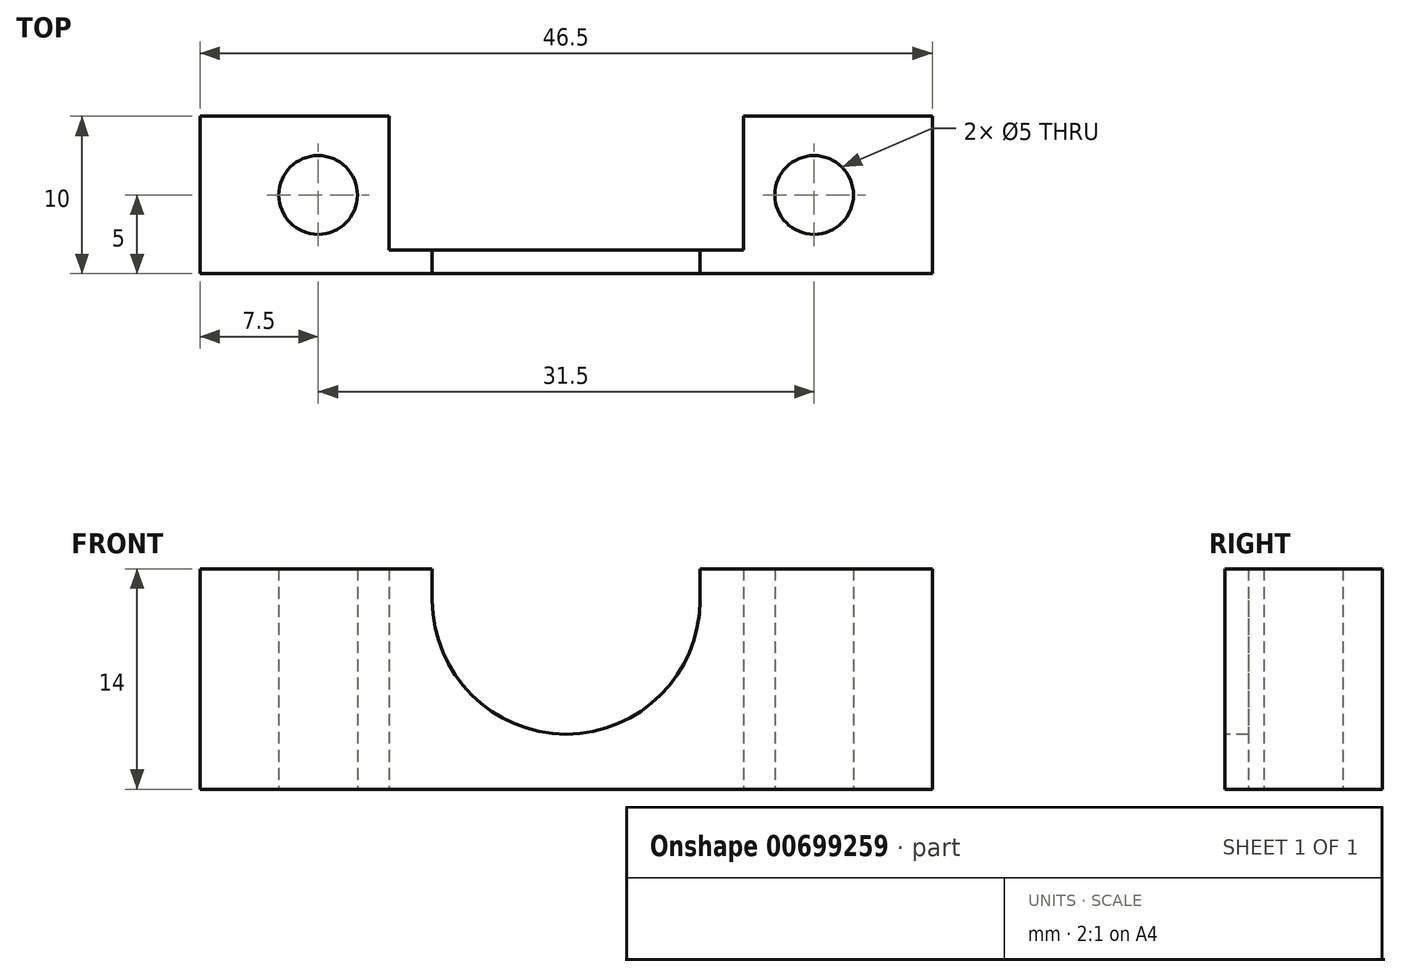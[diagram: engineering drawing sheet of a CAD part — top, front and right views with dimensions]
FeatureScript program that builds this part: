
annotation { "Feature Type Name" : "Feature", "Feature Type Description" : "" }
export const myFeature = defineFeature(function(context is Context, id is Id, definition is map)
    precondition{}
    {
        {
            var Q0;
            Q0=qCreatedBy(makeId("Top.planeOp"),FACE);
            var sketch = newSketch(context, id + "F0", { "sketchPlane" : qUnion([Q0])});
            skCircle(sketch, "E0", {"center": v(-15.75, 0) * mm, "radius": 2.5 * mm});
            skCircle(sketch, "E1", {"center": v(15.75, 0) * mm, "radius": 2.5 * mm});
            skLineSegment(sketch, "E2.bottom", {"start": v(-23.25, 5) * mm, "end": v(23.25, 5) * mm});
            skLineSegment(sketch, "E2.top", {"start": v(-23.25, -5) * mm, "end": v(23.25, -5) * mm});
            skLineSegment(sketch, "E2.left", {"start": v(-23.25, 5) * mm, "end": v(-23.25, -5) * mm});
            skLineSegment(sketch, "E2.right", {"start": v(23.25, 5) * mm, "end": v(23.25, -5) * mm});
            skLineSegment(sketch, "E3", {"start": v(-11.25, -3.5) * mm, "end": v(11.25, -3.5) * mm});
            skLineSegment(sketch, "E4", {"start": v(-11.25, -3.5) * mm, "end": v(-11.25, 5) * mm});
            skLineSegment(sketch, "E5", {"start": v(11.25, -3.5) * mm, "end": v(11.25, 5) * mm});
            skSolve(sketch);
        }
        {
            var Q0;
            Q0=makeQuery(id+"F0.imprint","IMPRINT",FACE,{"disambiguationData":[TD([[makeQuery(id+"F0.imprint","IMPRINT",EDGE,{"derivedFrom":sQuery(id+"F0.wireOp",EDGE,"E0")}),-1.0]])]});
            extrude(context, id + "F1", {"entities" : qUnion([Q0]), "depth" : 14 * mm, "offsetDistance" : 25 * mm});
        }
        {
            var Q0;
            Q0=makeQuery(id+"F1.opExtrude","SWEPT_FACE",FACE,{"disambiguationData":[OSD([sQuery(id+"F0.wireOp",EDGE,"E2.top")])]});
            var sketch = newSketch(context, id + "F2", { "sketchPlane" : qUnion([Q0])});
            skArc(sketch, "E6", {"start": v(-8.5, 12) * mm, "mid": v(0, 3.5) * mm, "end": v(8.5, 12) * mm});
            skLineSegment(sketch, "E7", {"start": v(-8.5, 12) * mm, "end": v(-8.5, 14) * mm});
            skLineSegment(sketch, "E8", {"start": v(8.5, 12) * mm, "end": v(8.5, 14) * mm});
            skLineSegment(sketch, "E9", {"start": v(-8.5, 14) * mm, "end": v(8.5, 14) * mm});
            skSolve(sketch);
        }
        {
            var Q0;
            Q0 = qSketchRegion(id + "F2", true);
            extrude(context, id + "F3", {"entities" : qUnion([Q0]), "operationType" : NewBodyOperationType.REMOVE, "oppositeDirection" : true, "depth" : 25 * mm, "offsetDistance" : 25 * mm});
        }
    });
